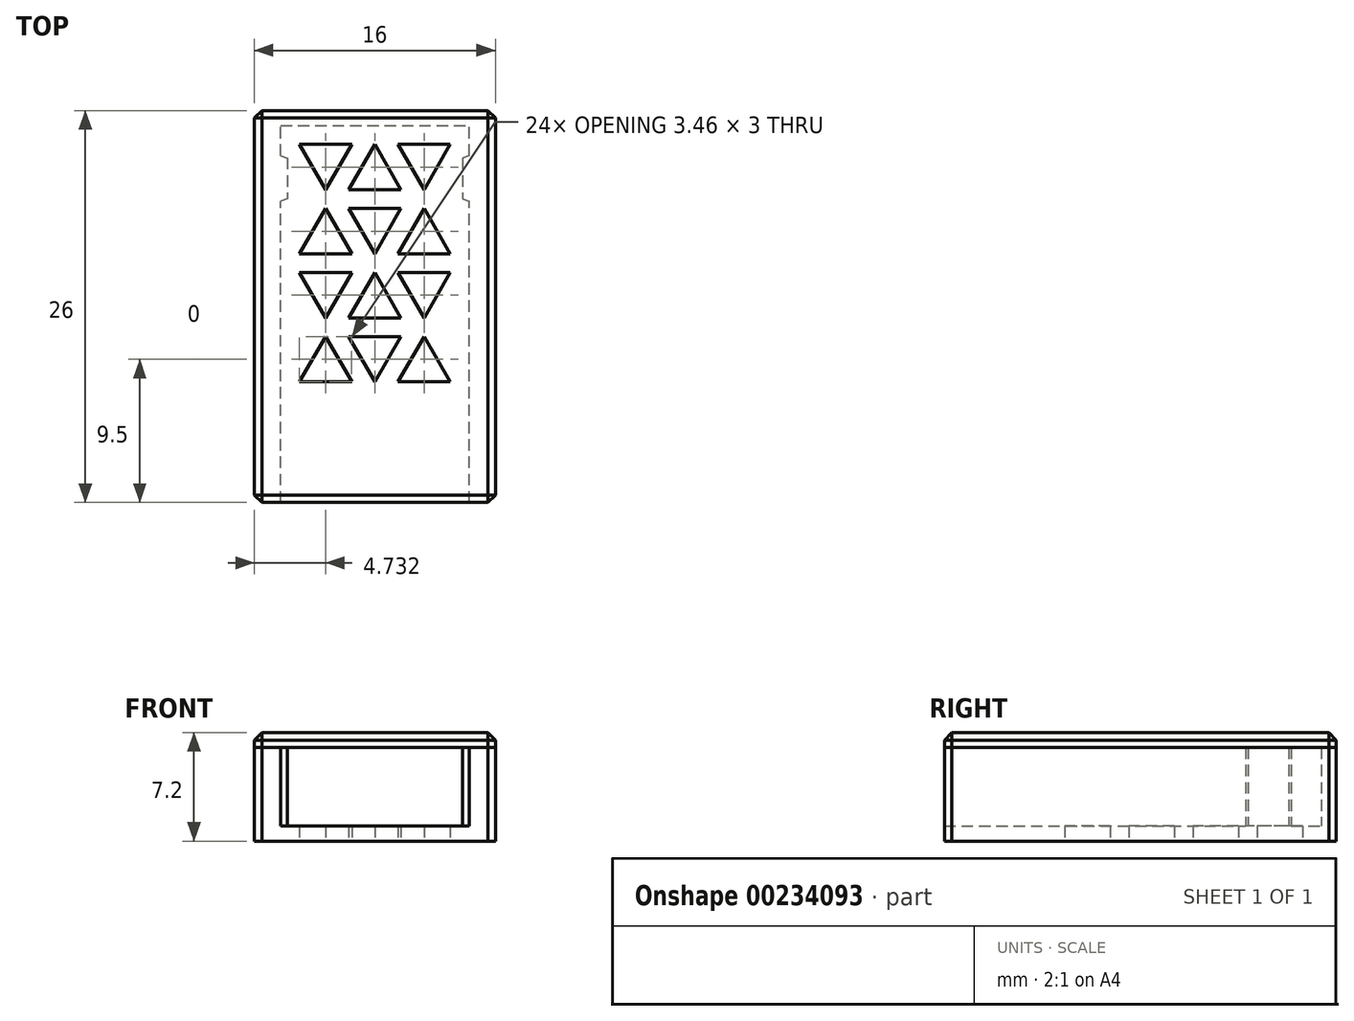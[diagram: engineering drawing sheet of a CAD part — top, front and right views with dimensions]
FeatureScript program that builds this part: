
annotation { "Feature Type Name" : "Feature", "Feature Type Description" : "" }
export const myFeature = defineFeature(function(context is Context, id is Id, definition is map)
    precondition{}
    {
        {
            var Q0;
            Q0=qCreatedBy(makeId("Top.planeOp"),FACE);
            cPlane(context, id + "F0", {"entities" : qUnion([Q0]), "cplaneType" : CPlaneType.OFFSET, "offset" : 1 * mm, "oppositeDirection" : true, "width" : 150 * mm, "height" : 150 * mm});
        }
        {
            var Q0;
            Q0=qCreatedBy(makeId("Front.planeOp"),FACE);
            var sketch = newSketch(context, id + "F1", { "sketchPlane" : qUnion([Q0])});
            skLineSegment(sketch, "E0.bottom", {"start": v(-6.25, 6.2) * mm, "end": v(6.25, 6.2) * mm});
            skLineSegment(sketch, "E0.top", {"start": v(-6.25, 1) * mm, "end": v(6.25, 1) * mm});
            skLineSegment(sketch, "E0.left", {"start": v(-6.25, 6.2) * mm, "end": v(-6.25, 1) * mm});
            skLineSegment(sketch, "E0.right", {"start": v(6.25, 6.2) * mm, "end": v(6.25, 1) * mm});
            skLineSegment(sketch, "E1.bottom", {"start": v(-8, 6.2) * mm, "end": v(8, 6.2) * mm});
            skLineSegment(sketch, "E1.top", {"start": v(-8, 0) * mm, "end": v(8, 0) * mm});
            skLineSegment(sketch, "E1.left", {"start": v(-8, 6.2) * mm, "end": v(-8, 0) * mm});
            skLineSegment(sketch, "E1.right", {"start": v(8, 6.2) * mm, "end": v(8, 0) * mm});
            skSolve(sketch);
        }
        {
            var Q0;
            Q0=qCreatedBy(makeId("Top.planeOp"),FACE);
            var sketch = newSketch(context, id + "F2", { "sketchPlane" : qUnion([Q0])});
            skLineSegment(sketch, "E2", {"start": v(-6.25, -3) * mm, "end": v(-6.25, -6) * mm});
            skLineSegment(sketch, "E3", {"start": v(-6.25, -6) * mm, "end": v(-5.8, -5.85) * mm});
            skLineSegment(sketch, "E4", {"start": v(-5.8, -5.85) * mm, "end": v(-5.8, -3.15) * mm});
            skLineSegment(sketch, "E5", {"start": v(-5.8, -3.15) * mm, "end": v(-6.25, -3) * mm});
            skLineSegment(sketch, "E6.MirrorCS", {"start": v(5.8, -5.85) * mm, "end": v(5.8, -3.15) * mm});
            skLineSegment(sketch, "E7.MirrorCS", {"start": v(5.8, -3.15) * mm, "end": v(6.25, -3) * mm});
            skLineSegment(sketch, "E8.MirrorCS", {"start": v(6.25, -3) * mm, "end": v(6.25, -6) * mm});
            skLineSegment(sketch, "E9.MirrorCS", {"start": v(6.25, -6) * mm, "end": v(5.8, -5.85) * mm});
            skSolve(sketch);
        }
        {
            var Q0;
            Q0=makeQuery(id+"F1.imprint","IMPRINT",FACE,{"disambiguationData":[TD([[makeQuery(id+"F1.imprint","IMPRINT",EDGE,{"derivedFrom":sQuery(id+"F1.wireOp",EDGE,"E0.top")}),-1.0]])]});
            extrude(context, id + "F3", {"entities" : qUnion([Q0]), "depth" : 26 * mm});
        }
        {
            var Q0;
            Q0=makeQuery(id+"F1.imprint","IMPRINT",FACE,{"disambiguationData":[TD([[makeQuery(id+"F1.imprint","IMPRINT",EDGE,{"derivedFrom":sQuery(id+"F1.wireOp",EDGE,"E0.top")}),1.0]])]});
            extrude(context, id + "F4", {"entities" : qUnion([Q0]), "operationType" : NewBodyOperationType.ADD, "depth" : 1 * mm});
        }
        {
            var Q0;
            Q0=makeQuery(id+"F2.imprint","IMPRINT",FACE,{"disambiguationData":[TD([[makeQuery(id+"F2.imprint","IMPRINT",EDGE,{"derivedFrom":sQuery(id+"F2.wireOp",EDGE,"E2")}),1.0]])]});
            var Q1;
            Q1=makeQuery(id+"F2.imprint","IMPRINT",FACE,{"disambiguationData":[TD([[makeQuery(id+"F2.imprint","IMPRINT",EDGE,{"derivedFrom":sQuery(id+"F2.wireOp",EDGE,"E6.MirrorCS")}),-1.0]])]});
            extrude(context, id + "F5", {"entities" : qUnion([Q0, Q1]), "operationType" : NewBodyOperationType.ADD, "depth" : 6.2 * mm});
        }
        {
            var Q0;
            Q0=qCreatedBy(id+"F0.planeOp",FACE);
            var sketch = newSketch(context, id + "F6", { "sketchPlane" : qUnion([Q0])});
            skCircle(sketch, "E10.cCircle", {"center": v(-3.27, -3.25) * mm, "radius": 1 * mm, "construction": true});
            skLineSegment(sketch, "E10.0", {"start": v(-3.27, -5.25) * mm, "end": v(-5, -2.25) * mm});
            skLineSegment(sketch, "E10.1", {"start": v(-5, -2.25) * mm, "end": v(-1.54, -2.25) * mm});
            skLineSegment(sketch, "E10.2", {"start": v(-1.54, -2.25) * mm, "end": v(-3.27, -5.25) * mm});
            skPoint(sketch, "E10.0.midPoint", {"position": v(-4.13, -3.75) * mm});
            skLineSegment(sketch, "E11.MirrorCS", {"start": v(5, -2.25) * mm, "end": v(1.54, -2.25) * mm});
            skLineSegment(sketch, "E12.MirrorCS", {"start": v(1.54, -2.25) * mm, "end": v(3.27, -5.25) * mm});
            skLineSegment(sketch, "E13.MirrorCS", {"start": v(3.27, -5.25) * mm, "end": v(5, -2.25) * mm});
            skCircle(sketch, "E14.cCircle", {"center": v(0, -4.25) * mm, "radius": 1 * mm, "construction": true});
            skLineSegment(sketch, "E14.0", {"start": v(-1.73, -5.25) * mm, "end": v(0, -2.25) * mm});
            skLineSegment(sketch, "E14.1", {"start": v(0, -2.25) * mm, "end": v(1.73, -5.25) * mm});
            skLineSegment(sketch, "E14.2", {"start": v(1.73, -5.25) * mm, "end": v(-1.73, -5.25) * mm});
            skPoint(sketch, "E14.0.midPoint", {"position": v(-0.87, -3.75) * mm});
            skLineSegment(sketch, "E15", {"start": v(-5.98, -5.88) * mm, "end": v(5.9, -5.88) * mm, "construction": true});
            skLineSegment(sketch, "E16.MirrorCS", {"start": v(1.54, -9.5) * mm, "end": v(3.27, -6.5) * mm});
            skLineSegment(sketch, "E17.MirrorCS", {"start": v(3.27, -6.5) * mm, "end": v(5, -9.5) * mm});
            skLineSegment(sketch, "E18.MirrorCS", {"start": v(5, -9.5) * mm, "end": v(1.54, -9.5) * mm});
            skLineSegment(sketch, "E19.MirrorCS", {"start": v(0, -9.5) * mm, "end": v(1.73, -6.5) * mm});
            skLineSegment(sketch, "E20.MirrorCS", {"start": v(-1.73, -6.5) * mm, "end": v(0, -9.5) * mm});
            skLineSegment(sketch, "E21.MirrorCS", {"start": v(1.73, -6.5) * mm, "end": v(-1.73, -6.5) * mm});
            skLineSegment(sketch, "E22.MirrorCS", {"start": v(-1.54, -9.5) * mm, "end": v(-3.27, -6.5) * mm});
            skLineSegment(sketch, "E23.MirrorCS", {"start": v(-3.27, -6.5) * mm, "end": v(-5, -9.5) * mm});
            skLineSegment(sketch, "E24.MirrorCS", {"start": v(-5, -9.5) * mm, "end": v(-1.54, -9.5) * mm});
            skLineSegment(sketch, "E25", {"start": v(-6.07, -10.13) * mm, "end": v(6.1, -10.13) * mm, "construction": true});
            skLineSegment(sketch, "E26.MirrorCS", {"start": v(-3.27, -13.75) * mm, "end": v(-5, -10.75) * mm});
            skLineSegment(sketch, "E27.MirrorCS", {"start": v(-1.54, -10.75) * mm, "end": v(-3.27, -13.75) * mm});
            skLineSegment(sketch, "E28.MirrorCS", {"start": v(-5, -10.75) * mm, "end": v(-1.54, -10.75) * mm});
            skLineSegment(sketch, "E29.MirrorCS", {"start": v(-1.73, -13.75) * mm, "end": v(0, -10.75) * mm});
            skLineSegment(sketch, "E30.MirrorCS", {"start": v(1.73, -13.75) * mm, "end": v(-1.73, -13.75) * mm});
            skLineSegment(sketch, "E31.MirrorCS", {"start": v(0, -10.75) * mm, "end": v(1.73, -13.75) * mm});
            skLineSegment(sketch, "E32.MirrorCS", {"start": v(1.54, -10.75) * mm, "end": v(3.27, -13.75) * mm});
            skLineSegment(sketch, "E33.MirrorCS", {"start": v(5, -10.75) * mm, "end": v(1.54, -10.75) * mm});
            skLineSegment(sketch, "E34.MirrorCS", {"start": v(3.27, -13.75) * mm, "end": v(5, -10.75) * mm});
            skLineSegment(sketch, "E35.MirrorCS", {"start": v(-3.27, -15) * mm, "end": v(-5, -18) * mm});
            skLineSegment(sketch, "E36.MirrorCS", {"start": v(-5, -18) * mm, "end": v(-1.54, -18) * mm});
            skLineSegment(sketch, "E37.MirrorCS", {"start": v(-1.54, -18) * mm, "end": v(-3.27, -15) * mm});
            skLineSegment(sketch, "E38.MirrorCS", {"start": v(0, -18) * mm, "end": v(1.73, -15) * mm});
            skLineSegment(sketch, "E39.MirrorCS", {"start": v(-1.73, -15) * mm, "end": v(0, -18) * mm});
            skLineSegment(sketch, "E40.MirrorCS", {"start": v(1.73, -15) * mm, "end": v(-1.73, -15) * mm});
            skLineSegment(sketch, "E41.MirrorCS", {"start": v(1.54, -18) * mm, "end": v(3.27, -15) * mm});
            skLineSegment(sketch, "E42.MirrorCS", {"start": v(5, -18) * mm, "end": v(1.54, -18) * mm});
            skLineSegment(sketch, "E43.MirrorCS", {"start": v(3.27, -15) * mm, "end": v(5, -18) * mm});
            skSolve(sketch);
        }
        {
            var Q0;
            Q0=makeQuery(id+"F3.opExtrude","SWEPT_FACE",FACE,{"disambiguationData":[OSD([sQuery(id+"F1.wireOp",EDGE,"E1.top")])]});
            extrude(context, id + "F7", {"entities" : qUnion([Q0]), "oppositeDirection" : true, "depth" : 1 * mm});
        }
        {
            var Q0;
            Q0=makeQuery(id+"F7.opExtrude","SWEPT_BODY",BODY,{"disambiguationData":[OSD([sQuery(id+"F1.wireOp",EDGE,"E1.top")])]});
            transform(context, id + "F8", {"entities" : qUnion([Q0]), "transformType" : TransformType.TRANSLATION_3D, "dx" : 0 * mm, "dy" : 0 * mm, "dz" : 6.2 * mm, "makeCopy" : false});
        }
        {
            var Q0;
            Q0=makeQuery(id+"F7.opExtrude","CAP_EDGE",EDGE,{"disambiguationData":[OSD([sQuery(id+"F1.wireOp",EDGE,"E1.top"),sQuery(id+"F1.wireOp",EDGE,"E1.right")])],"isStart":false});
            var Q1;
            {var subQ0=sQuery(id+"F1.wireOp",EDGE,"E1.top");Q1=makeQuery(id+"F7.opExtrude","CAP_EDGE",EDGE,{"disambiguationData":[OSD([subQ0]),TDD([makeQuery(id+"F3.opExtrude","CAP_EDGE",EDGE,{"disambiguationData":[OSD([subQ0])],"isStart":false})])],"isStart":false});}
            var Q2;
            Q2=makeQuery(id+"F7.opExtrude","CAP_EDGE",EDGE,{"disambiguationData":[OSD([sQuery(id+"F1.wireOp",EDGE,"E1.top"),sQuery(id+"F1.wireOp",EDGE,"E1.left")])],"isStart":false});
            var Q3;
            {var subQ0=sQuery(id+"F1.wireOp",EDGE,"E1.top");Q3=makeQuery(id+"F7.opExtrude","CAP_EDGE",EDGE,{"disambiguationData":[OSD([subQ0]),TDD([makeQuery(id+"F3.opExtrude","CAP_EDGE",EDGE,{"disambiguationData":[OSD([subQ0])],"isStart":true})])],"isStart":false});}
            var Q4;
            Q4=makeQuery(id+"F3.opExtrude","CAP_EDGE",EDGE,{"disambiguationData":[OSD([sQuery(id+"F1.wireOp",EDGE,"E1.right")])],"isStart":false});
            var Q5;
            Q5=makeQuery(id+"F3.opExtrude","CAP_EDGE",EDGE,{"disambiguationData":[OSD([sQuery(id+"F1.wireOp",EDGE,"E1.left")])],"isStart":false});
            var Q6;
            Q6=makeQuery(id+"F3.opExtrude","CAP_EDGE",EDGE,{"disambiguationData":[OSD([sQuery(id+"F1.wireOp",EDGE,"E1.left")])],"isStart":true});
            var Q7;
            Q7=makeQuery(id+"F3.opExtrude","CAP_EDGE",EDGE,{"disambiguationData":[OSD([sQuery(id+"F1.wireOp",EDGE,"E1.right")])],"isStart":true});
            var Q8;
            {var subQ0=sQuery(id+"F1.wireOp",EDGE,"E1.right");var subQ1=sQuery(id+"F1.wireOp",EDGE,"E1.top");Q8=makeQuery(id+"F7.opExtrude","SWEPT_EDGE",EDGE,{"disambiguationData":[OSD([subQ1,subQ0]),TDD([makeQuery(id+"F3.opExtrude","CAP_VERTEX",VERTEX,{"disambiguationData":[OSD([subQ1,subQ0])],"isStart":true})])]});}
            var Q9;
            {var subQ0=sQuery(id+"F1.wireOp",EDGE,"E1.right");var subQ1=sQuery(id+"F1.wireOp",EDGE,"E1.top");Q9=makeQuery(id+"F7.opExtrude","SWEPT_EDGE",EDGE,{"disambiguationData":[OSD([subQ1,subQ0]),TDD([makeQuery(id+"F3.opExtrude","CAP_VERTEX",VERTEX,{"disambiguationData":[OSD([subQ1,subQ0])],"isStart":false})])]});}
            var Q10;
            {var subQ0=sQuery(id+"F1.wireOp",EDGE,"E1.left");var subQ1=sQuery(id+"F1.wireOp",EDGE,"E1.top");Q10=makeQuery(id+"F7.opExtrude","SWEPT_EDGE",EDGE,{"disambiguationData":[OSD([subQ1,subQ0]),TDD([makeQuery(id+"F3.opExtrude","CAP_VERTEX",VERTEX,{"disambiguationData":[OSD([subQ1,subQ0])],"isStart":false})])]});}
            var Q11;
            {var subQ0=sQuery(id+"F1.wireOp",EDGE,"E1.left");var subQ1=sQuery(id+"F1.wireOp",EDGE,"E1.top");Q11=makeQuery(id+"F7.opExtrude","SWEPT_EDGE",EDGE,{"disambiguationData":[OSD([subQ1,subQ0]),TDD([makeQuery(id+"F3.opExtrude","CAP_VERTEX",VERTEX,{"disambiguationData":[OSD([subQ1,subQ0])],"isStart":true})])]});}
            chamfer(context, id + "F9", {"entities" : qUnion([Q0, Q1, Q2, Q3, Q4, Q5, Q6, Q7, Q8, Q9, Q10, Q11]), "width" : .5 * mm, "tangentPropagation" : true});
        }
        {
            var Q0;
            Q0=makeQuery(id+"F6.imprint","IMPRINT",FACE,{"disambiguationData":[TD([[makeQuery(id+"F6.imprint","IMPRINT",EDGE,{"derivedFrom":sQuery(id+"F6.wireOp",EDGE,"E10.0")}),-1.0]])]});
            var Q1;
            Q1=makeQuery(id+"F6.imprint","IMPRINT",FACE,{"disambiguationData":[TD([[makeQuery(id+"F6.imprint","IMPRINT",EDGE,{"derivedFrom":sQuery(id+"F6.wireOp",EDGE,"E14.0")}),-1.0]])]});
            var Q2;
            Q2=makeQuery(id+"F6.imprint","IMPRINT",FACE,{"disambiguationData":[TD([[makeQuery(id+"F6.imprint","IMPRINT",EDGE,{"derivedFrom":sQuery(id+"F6.wireOp",EDGE,"E11.MirrorCS")}),1.0]])]});
            var Q3;
            Q3=makeQuery(id+"F6.imprint","IMPRINT",FACE,{"disambiguationData":[TD([[makeQuery(id+"F6.imprint","IMPRINT",EDGE,{"derivedFrom":sQuery(id+"F6.wireOp",EDGE,"E22.MirrorCS")}),1.0]])]});
            var Q4;
            Q4=makeQuery(id+"F6.imprint","IMPRINT",FACE,{"disambiguationData":[TD([[makeQuery(id+"F6.imprint","IMPRINT",EDGE,{"derivedFrom":sQuery(id+"F6.wireOp",EDGE,"E19.MirrorCS")}),1.0]])]});
            var Q5;
            Q5=makeQuery(id+"F6.imprint","IMPRINT",FACE,{"disambiguationData":[TD([[makeQuery(id+"F6.imprint","IMPRINT",EDGE,{"derivedFrom":sQuery(id+"F6.wireOp",EDGE,"E16.MirrorCS")}),-1.0]])]});
            var Q6;
            Q6=makeQuery(id+"F6.imprint","IMPRINT",FACE,{"disambiguationData":[TD([[makeQuery(id+"F6.imprint","IMPRINT",EDGE,{"derivedFrom":sQuery(id+"F6.wireOp",EDGE,"E32.MirrorCS")}),1.0]])]});
            var Q7;
            Q7=makeQuery(id+"F6.imprint","IMPRINT",FACE,{"disambiguationData":[TD([[makeQuery(id+"F6.imprint","IMPRINT",EDGE,{"derivedFrom":sQuery(id+"F6.wireOp",EDGE,"E29.MirrorCS")}),-1.0]])]});
            var Q8;
            Q8=makeQuery(id+"F6.imprint","IMPRINT",FACE,{"disambiguationData":[TD([[makeQuery(id+"F6.imprint","IMPRINT",EDGE,{"derivedFrom":sQuery(id+"F6.wireOp",EDGE,"E26.MirrorCS")}),-1.0]])]});
            var Q9;
            Q9=makeQuery(id+"F6.imprint","IMPRINT",FACE,{"disambiguationData":[TD([[makeQuery(id+"F6.imprint","IMPRINT",EDGE,{"derivedFrom":sQuery(id+"F6.wireOp",EDGE,"E35.MirrorCS")}),1.0]])]});
            var Q10;
            Q10=makeQuery(id+"F6.imprint","IMPRINT",FACE,{"disambiguationData":[TD([[makeQuery(id+"F6.imprint","IMPRINT",EDGE,{"derivedFrom":sQuery(id+"F6.wireOp",EDGE,"E38.MirrorCS")}),1.0]])]});
            var Q11;
            Q11=makeQuery(id+"F6.imprint","IMPRINT",FACE,{"disambiguationData":[TD([[makeQuery(id+"F6.imprint","IMPRINT",EDGE,{"derivedFrom":sQuery(id+"F6.wireOp",EDGE,"E41.MirrorCS")}),-1.0]])]});
            extrude(context, id + "F10", {"entities" : qUnion([Q0, Q1, Q2, Q3, Q4, Q5, Q6, Q7, Q8, Q9, Q10, Q11]), "operationType" : NewBodyOperationType.REMOVE, "depth" : 25 * mm});
        }
    });
